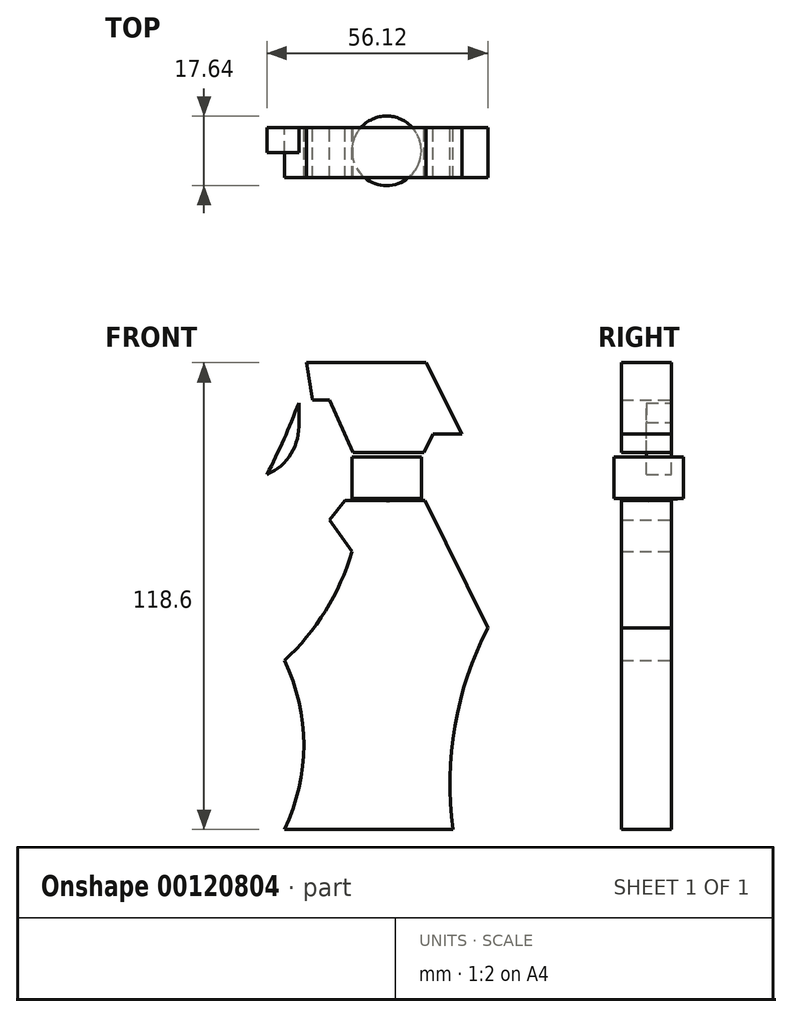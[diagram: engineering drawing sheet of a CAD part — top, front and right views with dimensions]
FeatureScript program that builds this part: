
annotation { "Feature Type Name" : "Feature", "Feature Type Description" : "" }
export const myFeature = defineFeature(function(context is Context, id is Id, definition is map)
    precondition{}
    {
        {
            var Q0;
            Q0=qCreatedBy(makeId("Front.planeOp"),FACE);
            var sketch = newSketch(context, id + "F0", { "sketchPlane" : qUnion([Q0])});
            skLineSegment(sketch, "E0", {"start": v(-23.04, -47.17) * mm, "end": v(19.85, -47.17) * mm});
            skArc(sketch, "E1", {"start": v(-23.04, -47.17) * mm, "mid": v(-18.09, -25.73) * mm, "end": v(-23.04, -4.29) * mm});
            skArc(sketch, "E2", {"start": v(-23.04, -4.29) * mm, "mid": v(-12.56, 8.38) * mm, "end": v(-5.88, 23.4) * mm});
            skArc(sketch, "E3", {"start": v(28.67, 4.04) * mm, "mid": v(20.3, -20.88) * mm, "end": v(19.85, -47.17) * mm});
            skLineSegment(sketch, "E4", {"start": v(28.67, 4.04) * mm, "end": v(12.74, 36.4) * mm});
            skLineSegment(sketch, "E5", {"start": v(12.74, 36.4) * mm, "end": v(-7.6, 36.4) * mm});
            skLineSegment(sketch, "E6", {"start": v(-7.6, 36.4) * mm, "end": v(-11.52, 31.49) * mm});
            skLineSegment(sketch, "E7", {"start": v(-11.52, 31.49) * mm, "end": v(-5.88, 23.4) * mm});
            skSolve(sketch);
        }
        {
            var Q0;
            Q0 = qSketchRegion(id + "F0", true);
            extrude(context, id + "F1", {"entities" : qUnion([Q0]), "depth" : 12.7 * mm});
        }
        {
            var Q0;
            Q0=qCreatedBy(makeId("Front.planeOp"),FACE);
            var sketch = newSketch(context, id + "F2", { "sketchPlane" : qUnion([Q0])});
            skLineSegment(sketch, "E8", {"start": v(2.94, 49.38) * mm, "end": v(2.94, 38.1) * mm});
            skLineSegment(sketch, "E9", {"start": v(2.94, 38.1) * mm, "end": v(2.94, 49.38) * mm});
            skLineSegment(sketch, "E10", {"start": v(2.94, 49.38) * mm, "end": v(11.76, 49.38) * mm});
            skLineSegment(sketch, "E11", {"start": v(11.76, 49.38) * mm, "end": v(11.76, 38.84) * mm});
            skLineSegment(sketch, "E12", {"start": v(11.76, 38.84) * mm, "end": v(2.94, 38.1) * mm});
            skSolve(sketch);
        }
        {
            var Q0;
            Q0 = qSketchRegion(id + "F2", true);
            var Q1;
            Q1=sQuery(id+"F2.wireOp",EDGE,"E9");
            revolve(context, id + "F3", {"entities" : qUnion([Q0]), "axis" : qUnion([Q1]), "revolveType" : RevolveType.FULL});
        }
        {
            var Q0;
            Q0=makeQuery(id+"F3.opRevolve","SWEPT_BODY",BODY,{"disambiguationData":[OSD([sQuery(id+"F2.wireOp",EDGE,"E9"),sQuery(id+"F2.wireOp",EDGE,"E10"),sQuery(id+"F2.wireOp",EDGE,"E11"),sQuery(id+"F2.wireOp",EDGE,"E12")])]});
            transform(context, id + "F4", {"entities" : qUnion([Q0]), "transformType" : TransformType.TRANSLATION_3D, "dx" : 0 * mm, "dy" : -5.88 * mm, "dz" : -1.96 * mm, "makeCopy" : false});
        }
        {
            var Q0;
            Q0=qCreatedBy(makeId("Front.planeOp"),FACE);
            var sketch = newSketch(context, id + "F5", { "sketchPlane" : qUnion([Q0])});
            skLineSegment(sketch, "E13", {"start": v(-15.93, 61.88) * mm, "end": v(-11.52, 61.88) * mm});
            skLineSegment(sketch, "E14", {"start": v(-11.52, 61.88) * mm, "end": v(-5.64, 48.64) * mm});
            skLineSegment(sketch, "E15", {"start": v(-5.64, 48.64) * mm, "end": v(12.5, 48.64) * mm});
            skLineSegment(sketch, "E16", {"start": v(12.5, 48.64) * mm, "end": v(14.7, 53.3) * mm});
            skLineSegment(sketch, "E17", {"start": v(14.7, 53.3) * mm, "end": v(22.05, 53.3) * mm});
            skLineSegment(sketch, "E18", {"start": v(22.05, 53.3) * mm, "end": v(12.99, 71.43) * mm});
            skLineSegment(sketch, "E19", {"start": v(12.99, 71.43) * mm, "end": v(-17.4, 71.43) * mm});
            skLineSegment(sketch, "E20", {"start": v(-17.4, 71.43) * mm, "end": v(-15.93, 61.88) * mm});
            skSolve(sketch);
        }
        {
            var Q0;
            Q0 = qSketchRegion(id + "F5", true);
            extrude(context, id + "F6", {"entities" : qUnion([Q0]), "depth" : 12.7 * mm});
        }
        {
            var Q0;
            Q0=qCreatedBy(makeId("Front.planeOp"),FACE);
            var sketch = newSketch(context, id + "F7", { "sketchPlane" : qUnion([Q0])});
            skArc(sketch, "E21", {"start": v(-27.45, 43) * mm, "mid": v(-21.3, 48.33) * mm, "end": v(-19.36, 56.24) * mm});
            skArc(sketch, "E22", {"start": v(-27.45, 43) * mm, "mid": v(-23.16, 51.97) * mm, "end": v(-19.36, 61.14) * mm});
            skLineSegment(sketch, "E23", {"start": v(-19.36, 61.14) * mm, "end": v(-19.36, 56.24) * mm});
            skSolve(sketch);
        }
        {
            var Q0;
            Q0 = qSketchRegion(id + "F7", true);
            extrude(context, id + "F8", {"entities" : qUnion([Q0]), "depth" : 6.35 * mm});
        }
    });
